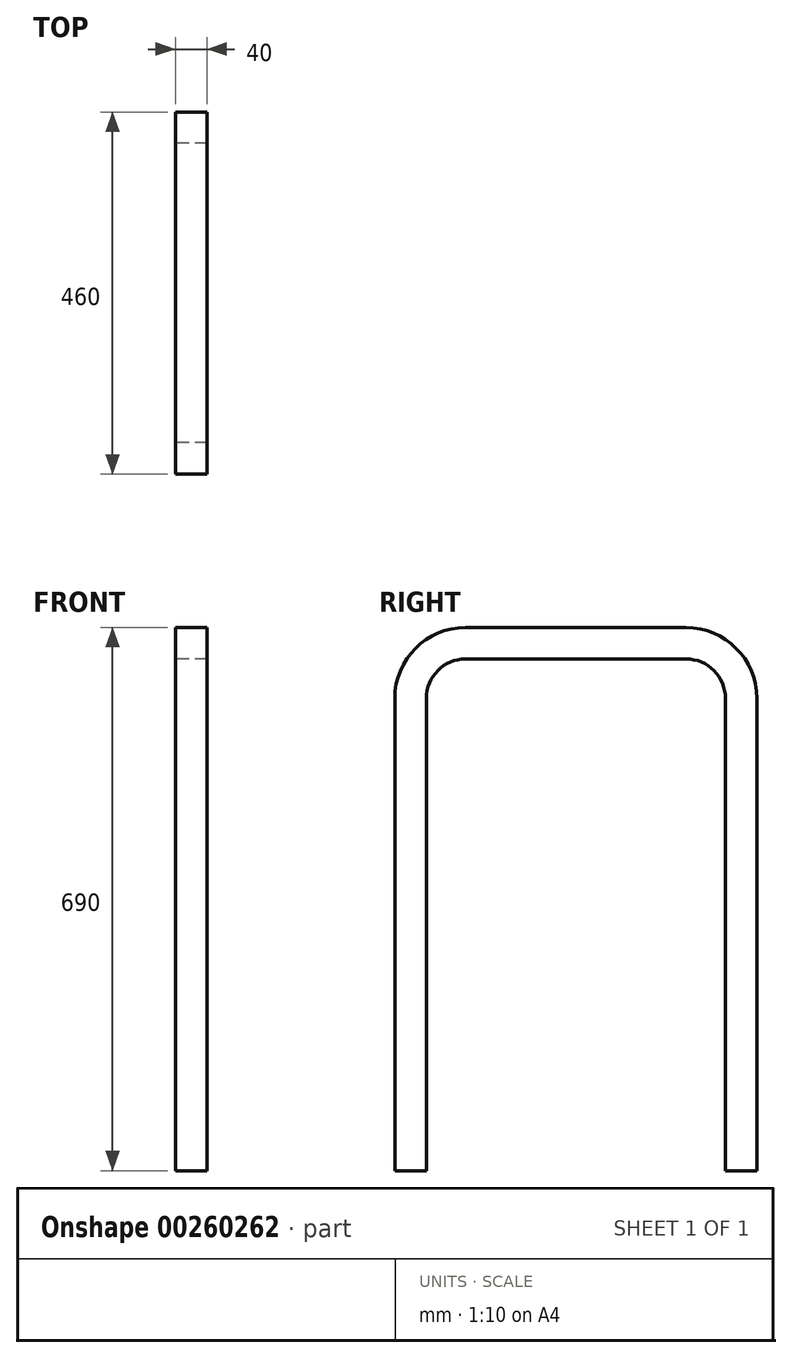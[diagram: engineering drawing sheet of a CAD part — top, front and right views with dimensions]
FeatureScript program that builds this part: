
annotation { "Feature Type Name" : "Feature", "Feature Type Description" : "" }
export const myFeature = defineFeature(function(context is Context, id is Id, definition is map)
    precondition{}
    {
        {
            var Q0;
            Q0=qCreatedBy(makeId("Right.planeOp"),FACE);
            var sketch = newSketch(context, id + "F0", { "sketchPlane" : qUnion([Q0])});
            skLineSegment(sketch, "E0", {"start": v(-190, 0) * mm, "end": v(-190, 600) * mm});
            skLineSegment(sketch, "E1", {"start": v(-140, 650) * mm, "end": v(140, 650) * mm});
            skLineSegment(sketch, "E2", {"start": v(190, 600) * mm, "end": v(190, 0) * mm});
            skLineSegment(sketch, "E3", {"start": v(190, 0) * mm, "end": v(230, 0) * mm});
            skLineSegment(sketch, "E4", {"start": v(230, 0) * mm, "end": v(230, 600) * mm});
            skLineSegment(sketch, "E5", {"start": v(140, 690) * mm, "end": v(-140, 690) * mm});
            skLineSegment(sketch, "E6", {"start": v(-230, 600) * mm, "end": v(-230, 0) * mm});
            skLineSegment(sketch, "E7", {"start": v(-230, 0) * mm, "end": v(-190, 0) * mm});
            skLineSegment(sketch, "E8", {"start": v(0, 650) * mm, "end": v(0, 690) * mm, "construction": true});
            skPoint(sketch, "E9.visualSharp", {"position": v(-190, 650) * mm});
            skArc(sketch, "E9.filletArc", {"start": v(-140, 650) * mm, "mid": v(-175.36, 635.36) * mm, "end": v(-190, 600) * mm});
            skPoint(sketch, "E10.visualSharp", {"position": v(190, 650) * mm});
            skArc(sketch, "E10.filletArc", {"start": v(190, 600) * mm, "mid": v(175.36, 635.36) * mm, "end": v(140, 650) * mm});
            skPoint(sketch, "E11.visualSharp", {"position": v(-230, 690) * mm});
            skArc(sketch, "E11.filletArc", {"start": v(-140, 690) * mm, "mid": v(-203.64, 663.64) * mm, "end": v(-230, 600) * mm});
            skPoint(sketch, "E12.visualSharp", {"position": v(230, 690) * mm});
            skArc(sketch, "E12.filletArc", {"start": v(230, 600) * mm, "mid": v(203.64, 663.64) * mm, "end": v(140, 690) * mm});
            skSolve(sketch);
        }
        {
            var Q0;
            Q0=makeQuery(id+"F0.imprint","IMPRINT",FACE,{"disambiguationData":[TD([[makeQuery(id+"F0.imprint","IMPRINT",EDGE,{"derivedFrom":sQuery(id+"F0.wireOp",EDGE,"E0")}),1.0]])]});
            extrude(context, id + "F1", {"entities" : qUnion([Q0]), "endBound" : BoundingType.SYMMETRIC, "depth" : 40 * mm, "offsetDistance" : 25 * mm});
        }
    });
